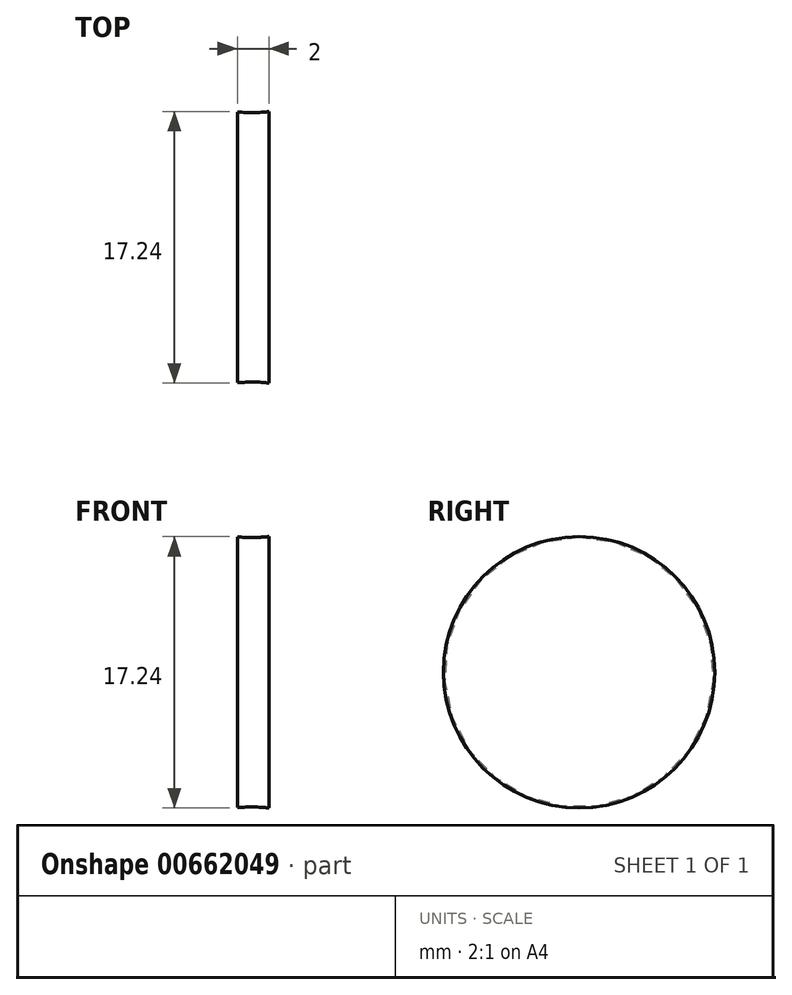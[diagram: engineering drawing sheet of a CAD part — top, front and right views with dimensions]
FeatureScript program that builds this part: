
annotation { "Feature Type Name" : "Feature", "Feature Type Description" : "" }
export const myFeature = defineFeature(function(context is Context, id is Id, definition is map)
    precondition{}
    {
        {
            var Q0;
            Q0=qCreatedBy(makeId("Front.planeOp"),FACE);
            var sketch = newSketch(context, id + "F0", { "sketchPlane" : qUnion([Q0])});
            skLineSegment(sketch, "E0", {"start": v(39.5, 0) * mm, "end": v(39.5, 10.63) * mm});
            skFitSpline(sketch, "E1", {"points": [v(39.5, 10.63) * mm, v(-33.05, 43.4) * mm], "startDerivative": vector(-40.98, -4.22) * mm, "endDerivative": vector(-46.5, 0) * mm});
            skLineSegment(sketch, "E2", {"start": v(-33.05, 43.4) * mm, "end": v(-234.17, 43.4) * mm});
            skLineSegment(sketch, "E3", {"start": v(-234.17, 43.4) * mm, "end": v(-234.17, 0) * mm});
            skLineSegment(sketch, "E4.0", {"start": v(-232.17, 41.4) * mm, "end": v(-232.17, 0) * mm});
            skLineSegment(sketch, "E4.1", {"start": v(-33.05, 41.4) * mm, "end": v(-232.17, 41.4) * mm});
            skFitSpline(sketch, "E4.2", {"points": [v(39.7, 8.64) * mm, v(39.15, 8.59) * mm, v(38.04, 8.57) * mm, v(35.71, 8.83) * mm, v(32.55, 9.63) * mm, v(28.35, 11.2) * mm, v(22.23, 13.99) * mm, v(13.77, 18.5) * mm, v(2.92, 24.75) * mm, v(-7.97, 31.05) * mm, v(-16.5, 35.64) * mm, v(-22.64, 38.51) * mm, v(-26.79, 40.15) * mm, v(-30.37, 41.18) * mm, v(-32.26, 41.4) * mm, v(-33.05, 41.4) * mm]});
            skLineSegment(sketch, "E4.3", {"start": v(37.5, 0) * mm, "end": v(37.5, 8.64) * mm});
            skLineSegment(sketch, "E5", {"start": v(-234.17, 0) * mm, "end": v(-232.17, 0) * mm});
            skLineSegment(sketch, "E6", {"start": v(37.5, 0) * mm, "end": v(39.5, 0) * mm});
            skLineSegment(sketch, "E7", {"start": v(-97.25, 0) * mm, "end": v(47.1, 0) * mm});
            skSolve(sketch);
        }
        {
            var Q0;
            {var subQ0=sQuery(id+"F0.wireOp",EDGE,"E0");Q0=makeQuery(id+"F0.imprint","IMPRINT",FACE,{"disambiguationData":[TD([[makeQuery(id+"F0.imprint","IMPRINT",EDGE,{"derivedFrom":subQ0}),1.0]])]});}
            var Q1;
            Q1=sQuery(id+"F0.wireOp",EDGE,"E7");
            revolve(context, id + "F1", {"entities" : qUnion([Q0]), "axis" : qUnion([Q1]), "revolveType" : RevolveType.FULL});
        }
    });
